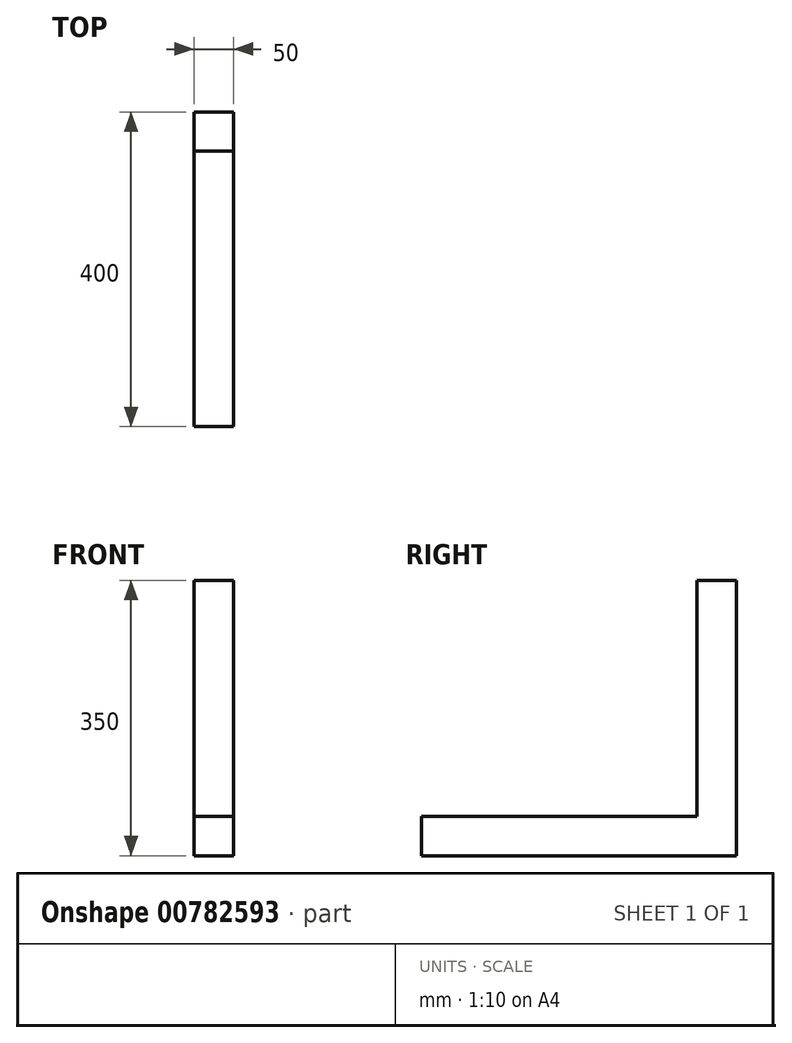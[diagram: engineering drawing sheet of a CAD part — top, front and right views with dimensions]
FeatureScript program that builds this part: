
annotation { "Feature Type Name" : "Feature", "Feature Type Description" : "" }
export const myFeature = defineFeature(function(context is Context, id is Id, definition is map)
    precondition{}
    {
        {
            var Q0;
            Q0=qCreatedBy(makeId("Front.planeOp"),FACE);
            var sketch = newSketch(context, id + "F0", { "sketchPlane" : qUnion([Q0])});
            skLineSegment(sketch, "E0.bottom", {"start": v(0, 0) * mm, "end": v(50, 0) * mm});
            skLineSegment(sketch, "E0.top", {"start": v(0, 50) * mm, "end": v(50, 50) * mm});
            skLineSegment(sketch, "E0.left", {"start": v(0, 0) * mm, "end": v(0, 50) * mm});
            skLineSegment(sketch, "E0.right", {"start": v(50, 0) * mm, "end": v(50, 50) * mm});
            skSolve(sketch);
        }
        {
            var Q0;
            Q0=qSketchRegion(id+"F0",true);
            extrude(context, id + "F1", {"entities" : qUnion([Q0]), "depth" : 350 * mm, "offsetDistance" : 25 * mm});
        }
        {
            var Q0;
            Q0=qCreatedBy(makeId("Top.planeOp"),FACE);
            var sketch = newSketch(context, id + "F2", { "sketchPlane" : qUnion([Q0])});
            skLineSegment(sketch, "E1.bottom", {"start": v(0, 0) * mm, "end": v(50, 0) * mm});
            skLineSegment(sketch, "E1.top", {"start": v(0, 50) * mm, "end": v(50, 50) * mm});
            skLineSegment(sketch, "E1.left", {"start": v(0, 0) * mm, "end": v(0, 50) * mm});
            skLineSegment(sketch, "E1.right", {"start": v(50, 0) * mm, "end": v(50, 50) * mm});
            skSolve(sketch);
        }
        {
            var Q0;
            Q0=qSketchRegion(id+"F2",true);
            extrude(context, id + "F3", {"entities" : qUnion([Q0]), "operationType" : NewBodyOperationType.ADD, "depth" : 350 * mm, "offsetDistance" : 25 * mm});
        }
    });
